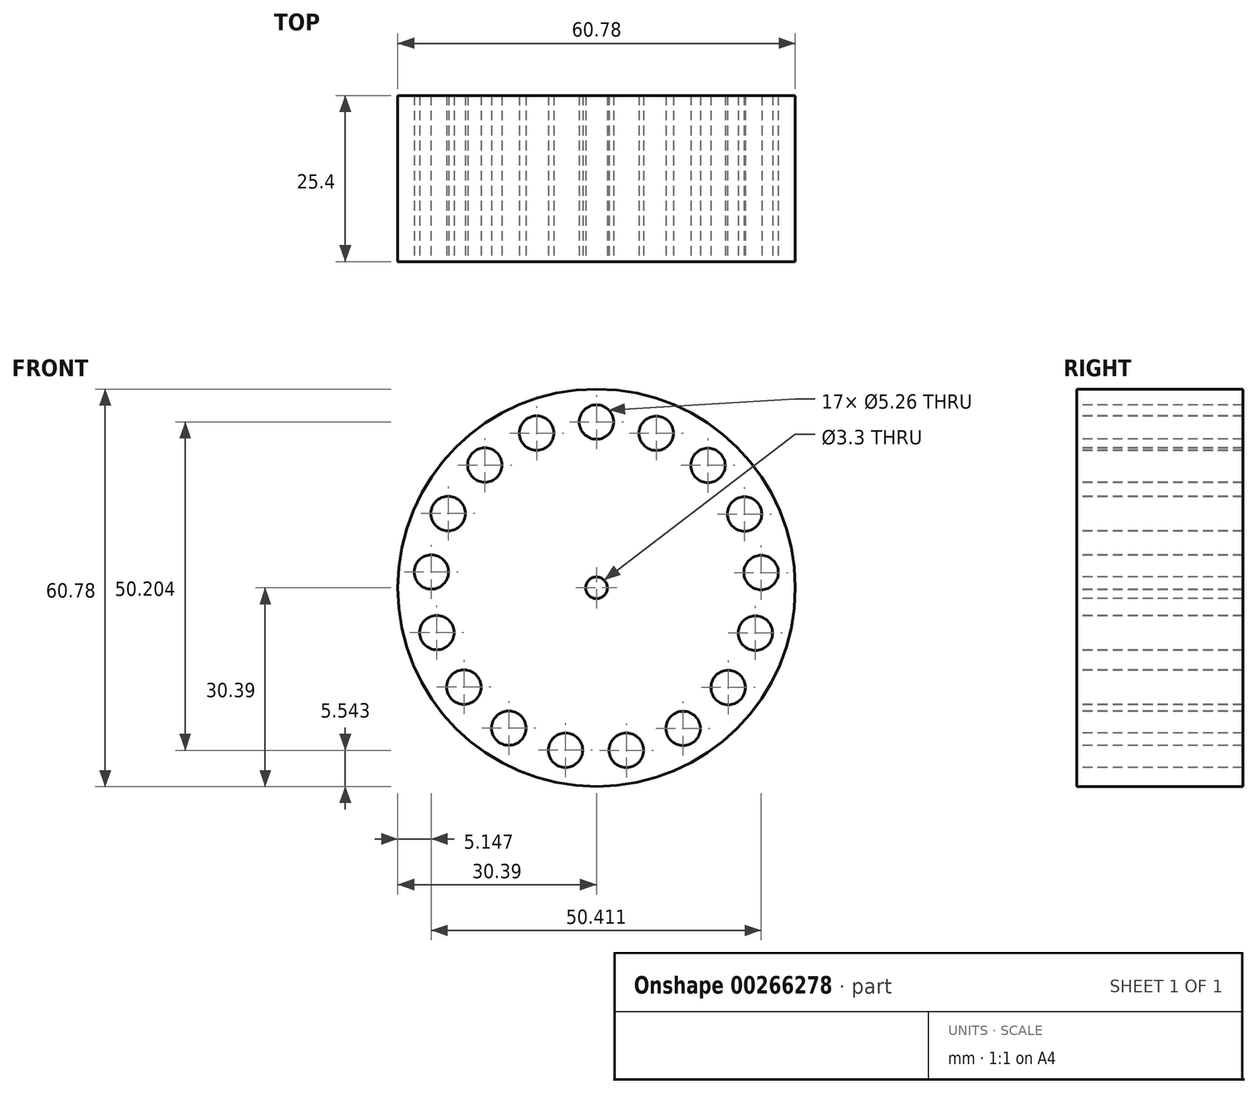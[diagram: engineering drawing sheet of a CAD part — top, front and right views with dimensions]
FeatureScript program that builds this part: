
annotation { "Feature Type Name" : "Feature", "Feature Type Description" : "" }
export const myFeature = defineFeature(function(context is Context, id is Id, definition is map)
    precondition{}
    {
        {
            var Q0;
            Q0=qCreatedBy(makeId("Front.planeOp"),FACE);
            var sketch = newSketch(context, id + "F0", { "sketchPlane" : qUnion([Q0])});
            skCircle(sketch, "E0", {"center": v(0, 0) * mm, "radius": 30.4 * mm});
            skSolve(sketch);
        }
        {
            var Q0;
            Q0 = qSketchRegion(id + "F0", true);
            extrude(context, id + "F1", {"entities" : qUnion([Q0]), "depth" : 25.4 * mm});
        }
        {
            var Q0;
            Q0=makeQuery(id+"F1.opExtrude","CAP_FACE",FACE,{"disambiguationData":[OSD([sQuery(id+"F0.wireOp",EDGE,"E0")])],"isStart":false});
            var sketch = newSketch(context, id + "F2", { "sketchPlane" : qUnion([Q0])});
            skCircle(sketch, "E1", {"center": v(0, 25.36) * mm, "radius": 2.63 * mm});
            skCircle(sketch, "E2.1.0", {"center": v(-9.15, 23.66) * mm, "radius": 2.63 * mm});
            skCircle(sketch, "E2.2.0", {"center": v(-17.06, 18.78) * mm, "radius": 2.63 * mm});
            skCircle(sketch, "E2.3.0", {"center": v(-22.68, 11.36) * mm, "radius": 2.63 * mm});
            skCircle(sketch, "E2.4.0", {"center": v(-25.24, 2.42) * mm, "radius": 2.63 * mm});
            skCircle(sketch, "E2.5.0", {"center": v(-24.4, -6.84) * mm, "radius": 2.63 * mm});
            skCircle(sketch, "E2.6.0", {"center": v(-20.27, -15.18) * mm, "radius": 2.63 * mm});
            skPoint(sketch, "E2.center", {"position": v(-0.04, 0.04) * mm});
            skCircle(sketch, "E3.1.7.0", {"center": v(-13.4, -21.46) * mm, "radius": 2.63 * mm});
            skCircle(sketch, "E4.1.8.0", {"center": v(-4.73, -24.83) * mm, "radius": 2.63 * mm});
            skCircle(sketch, "E5.1.9.0", {"center": v(4.57, -24.85) * mm, "radius": 2.63 * mm});
            skCircle(sketch, "E6.1.10.0", {"center": v(13.25, -21.5) * mm, "radius": 2.63 * mm});
            skCircle(sketch, "E6.1.11.0", {"center": v(20.13, -15.25) * mm, "radius": 2.63 * mm});
            skCircle(sketch, "E6.1.12.0", {"center": v(24.3, -6.92) * mm, "radius": 2.63 * mm});
            skCircle(sketch, "E6.1.13.0", {"center": v(25.17, 2.34) * mm, "radius": 2.63 * mm});
            skCircle(sketch, "E6.1.14.0", {"center": v(22.64, 11.29) * mm, "radius": 2.63 * mm});
            skCircle(sketch, "E6.1.15.0", {"center": v(17.04, 18.72) * mm, "radius": 2.63 * mm});
            skCircle(sketch, "E6.1.16.0", {"center": v(9.14, 23.63) * mm, "radius": 2.63 * mm});
            skSolve(sketch);
        }
        {
            var Q0;
            Q0=makeQuery(id+"F2.imprint","IMPRINT",FACE,{"disambiguationData":[TD([[makeQuery(id+"F2.imprint","IMPRINT",EDGE,{"derivedFrom":sQuery(id+"F2.wireOp",EDGE,"E2.1.0")}),1.0]])]});
            var Q1;
            Q1=makeQuery(id+"F2.imprint","IMPRINT",FACE,{"disambiguationData":[TD([[makeQuery(id+"F2.imprint","IMPRINT",EDGE,{"derivedFrom":sQuery(id+"F2.wireOp",EDGE,"E1")}),1.0]])]});
            var Q2;
            Q2=makeQuery(id+"F2.imprint","IMPRINT",FACE,{"disambiguationData":[TD([[makeQuery(id+"F2.imprint","IMPRINT",EDGE,{"derivedFrom":sQuery(id+"F2.wireOp",EDGE,"E2.9.0")}),1.0]])]});
            var Q3;
            Q3=makeQuery(id+"F2.imprint","IMPRINT",FACE,{"disambiguationData":[TD([[makeQuery(id+"F2.imprint","IMPRINT",EDGE,{"derivedFrom":sQuery(id+"F2.wireOp",EDGE,"E2.8.0")}),1.0]])]});
            var Q4;
            Q4=makeQuery(id+"F2.imprint","IMPRINT",FACE,{"disambiguationData":[TD([[makeQuery(id+"F2.imprint","IMPRINT",EDGE,{"derivedFrom":sQuery(id+"F2.wireOp",EDGE,"E2.7.0")}),1.0]])]});
            var Q5;
            Q5=makeQuery(id+"F2.imprint","IMPRINT",FACE,{"disambiguationData":[TD([[makeQuery(id+"F2.imprint","IMPRINT",EDGE,{"derivedFrom":sQuery(id+"F2.wireOp",EDGE,"E2.6.0")}),1.0]])]});
            var Q6;
            Q6=makeQuery(id+"F2.imprint","IMPRINT",FACE,{"disambiguationData":[TD([[makeQuery(id+"F2.imprint","IMPRINT",EDGE,{"derivedFrom":sQuery(id+"F2.wireOp",EDGE,"E2.5.0")}),1.0]])]});
            var Q7;
            Q7=makeQuery(id+"F2.imprint","IMPRINT",FACE,{"disambiguationData":[TD([[makeQuery(id+"F2.imprint","IMPRINT",EDGE,{"derivedFrom":sQuery(id+"F2.wireOp",EDGE,"E2.4.0")}),1.0]])]});
            var Q8;
            Q8=makeQuery(id+"F2.imprint","IMPRINT",FACE,{"disambiguationData":[TD([[makeQuery(id+"F2.imprint","IMPRINT",EDGE,{"derivedFrom":sQuery(id+"F2.wireOp",EDGE,"E2.3.0")}),1.0]])]});
            var Q9;
            Q9=makeQuery(id+"F2.imprint","IMPRINT",FACE,{"disambiguationData":[TD([[makeQuery(id+"F2.imprint","IMPRINT",EDGE,{"derivedFrom":sQuery(id+"F2.wireOp",EDGE,"E2.2.0")}),1.0]])]});
            var Q10;
            Q10=makeQuery(id+"F2.imprint","IMPRINT",FACE,{"disambiguationData":[TD([[makeQuery(id+"F2.imprint","IMPRINT",EDGE,{"derivedFrom":sQuery(id+"F2.wireOp",EDGE,"E4.1.8.0")}),1.0]])]});
            var Q11;
            Q11=makeQuery(id+"F2.imprint","IMPRINT",FACE,{"disambiguationData":[TD([[makeQuery(id+"F2.imprint","IMPRINT",EDGE,{"derivedFrom":sQuery(id+"F2.wireOp",EDGE,"E3.1.7.0")}),1.0]])]});
            var Q12;
            Q12=makeQuery(id+"F2.imprint","IMPRINT",FACE,{"disambiguationData":[TD([[makeQuery(id+"F2.imprint","IMPRINT",EDGE,{"derivedFrom":sQuery(id+"F2.wireOp",EDGE,"E5.1.9.0")}),1.0]])]});
            var Q13;
            Q13=makeQuery(id+"F2.imprint","IMPRINT",FACE,{"disambiguationData":[TD([[makeQuery(id+"F2.imprint","IMPRINT",EDGE,{"derivedFrom":sQuery(id+"F2.wireOp",EDGE,"E6.1.17.0")}),1.0]])]});
            var Q14;
            Q14=makeQuery(id+"F2.imprint","IMPRINT",FACE,{"disambiguationData":[TD([[makeQuery(id+"F2.imprint","IMPRINT",EDGE,{"derivedFrom":sQuery(id+"F2.wireOp",EDGE,"E6.1.16.0")}),1.0]])]});
            var Q15;
            Q15=makeQuery(id+"F2.imprint","IMPRINT",FACE,{"disambiguationData":[TD([[makeQuery(id+"F2.imprint","IMPRINT",EDGE,{"derivedFrom":sQuery(id+"F2.wireOp",EDGE,"E6.1.15.0")}),1.0]])]});
            var Q16;
            Q16=makeQuery(id+"F2.imprint","IMPRINT",FACE,{"disambiguationData":[TD([[makeQuery(id+"F2.imprint","IMPRINT",EDGE,{"derivedFrom":sQuery(id+"F2.wireOp",EDGE,"E6.1.14.0")}),1.0]])]});
            var Q17;
            Q17=makeQuery(id+"F2.imprint","IMPRINT",FACE,{"disambiguationData":[TD([[makeQuery(id+"F2.imprint","IMPRINT",EDGE,{"derivedFrom":sQuery(id+"F2.wireOp",EDGE,"E6.1.13.0")}),1.0]])]});
            var Q18;
            Q18=makeQuery(id+"F2.imprint","IMPRINT",FACE,{"disambiguationData":[TD([[makeQuery(id+"F2.imprint","IMPRINT",EDGE,{"derivedFrom":sQuery(id+"F2.wireOp",EDGE,"E6.1.12.0")}),1.0]])]});
            var Q19;
            Q19=makeQuery(id+"F2.imprint","IMPRINT",FACE,{"disambiguationData":[TD([[makeQuery(id+"F2.imprint","IMPRINT",EDGE,{"derivedFrom":sQuery(id+"F2.wireOp",EDGE,"E6.1.11.0")}),1.0]])]});
            var Q20;
            Q20=makeQuery(id+"F2.imprint","IMPRINT",FACE,{"disambiguationData":[TD([[makeQuery(id+"F2.imprint","IMPRINT",EDGE,{"derivedFrom":sQuery(id+"F2.wireOp",EDGE,"E6.1.10.0")}),1.0]])]});
            var Q21;
            Q21=sQuery(id+"F2.wireOp",EDGE,"E1");
            var Q22;
            Q22=sQuery(id+"F2.wireOp",EDGE,"E2.1.0");
            var Q23;
            Q23=sQuery(id+"F2.wireOp",EDGE,"E2.9.0");
            var Q24;
            Q24=sQuery(id+"F2.wireOp",EDGE,"E2.8.0");
            var Q25;
            Q25=sQuery(id+"F2.wireOp",EDGE,"E2.7.0");
            var Q26;
            Q26=sQuery(id+"F2.wireOp",EDGE,"E2.6.0");
            var Q27;
            Q27=sQuery(id+"F2.wireOp",EDGE,"E2.4.0");
            var Q28;
            Q28=sQuery(id+"F2.wireOp",EDGE,"E2.5.0");
            var Q29;
            Q29=sQuery(id+"F2.wireOp",EDGE,"E2.3.0");
            var Q30;
            Q30=sQuery(id+"F2.wireOp",EDGE,"E2.2.0");
            extrude(context, id + "F3", {"entities" : qUnion([Q0, Q1, Q2, Q3, Q4, Q5, Q6, Q7, Q8, Q9, Q10, Q11, Q12, Q13, Q14, Q15, Q16, Q17, Q18, Q19, Q20]), "operationType" : NewBodyOperationType.REMOVE, "surfaceEntities" : qUnion([Q21, Q22, Q23, Q24, Q25, Q26, Q27, Q28, Q29, Q30]), "oppositeDirection" : true, "depth" : 35.3 * mm});
        }
        {
            var Q0;
            Q0=makeQuery(id+"F1.opExtrude","CAP_FACE",FACE,{"disambiguationData":[OSD([sQuery(id+"F0.wireOp",EDGE,"E0")])],"isStart":false});
            var sketch = newSketch(context, id + "F4", { "sketchPlane" : qUnion([Q0])});
            skCircle(sketch, "E7", {"center": v(0, 0) * mm, "radius": 1.65 * mm});
            skSolve(sketch);
        }
        {
            var Q0;
            Q0 = qSketchRegion(id + "F4", true);
            extrude(context, id + "F5", {"entities" : qUnion([Q0]), "operationType" : NewBodyOperationType.REMOVE, "oppositeDirection" : true, "depth" : 25.4 * mm});
        }
    });
